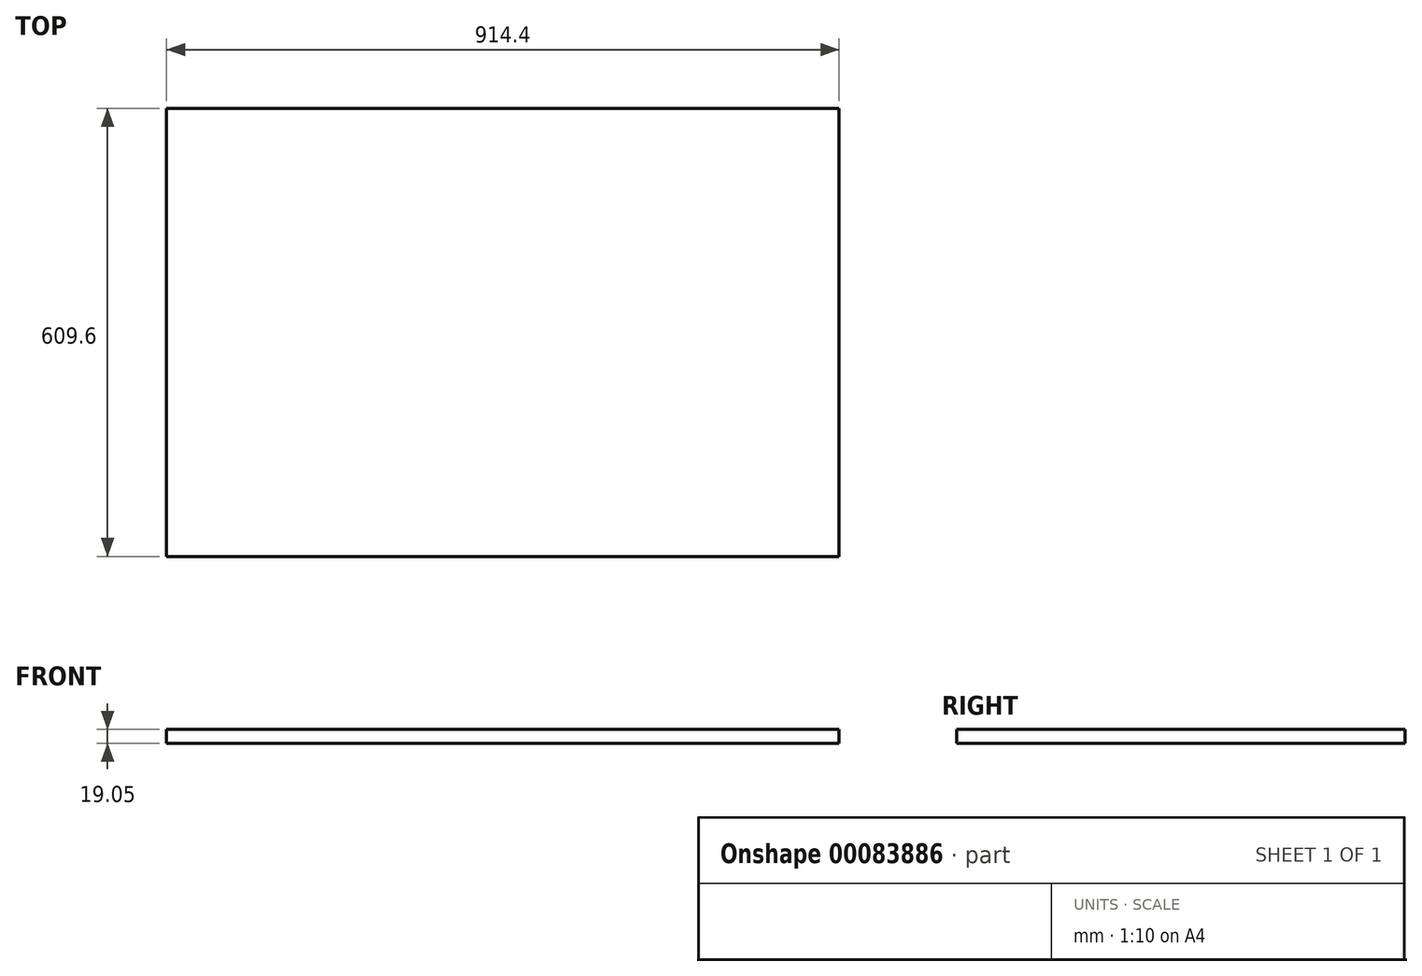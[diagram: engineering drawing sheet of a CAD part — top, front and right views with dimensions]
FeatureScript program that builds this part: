
annotation { "Feature Type Name" : "Feature", "Feature Type Description" : "" }
export const myFeature = defineFeature(function(context is Context, id is Id, definition is map)
    precondition{}
    {
        {
            var Q0;
            Q0=qCreatedBy(makeId("Top.planeOp"),FACE);
            var sketch = newSketch(context, id + "F0", { "sketchPlane" : qUnion([Q0])});
            skLineSegment(sketch, "E0.bottom", {"start": v(457.2, 304.8) * mm, "end": v(-457.2, 304.8) * mm});
            skLineSegment(sketch, "E0.top", {"start": v(457.2, -304.8) * mm, "end": v(-457.2, -304.8) * mm});
            skLineSegment(sketch, "E0.left", {"start": v(457.2, 304.8) * mm, "end": v(457.2, -304.8) * mm});
            skLineSegment(sketch, "E0.right", {"start": v(-457.2, 304.8) * mm, "end": v(-457.2, -304.8) * mm});
            skPoint(sketch, "E0.middle", {"position": v(0, 0) * mm});
            skSolve(sketch);
        }
        {
            var Q0;
            Q0=makeQuery(id+"F0.imprint","IMPRINT",FACE,{"disambiguationData":[TD([[makeQuery(id+"F0.imprint","IMPRINT",EDGE,{"derivedFrom":sQuery(id+"F0.wireOp",EDGE,"E0.bottom")}),1.0]])]});
            extrude(context, id + "F1", {"entities" : qUnion([Q0]), "depth" : 19.05 * mm});
        }
    });
